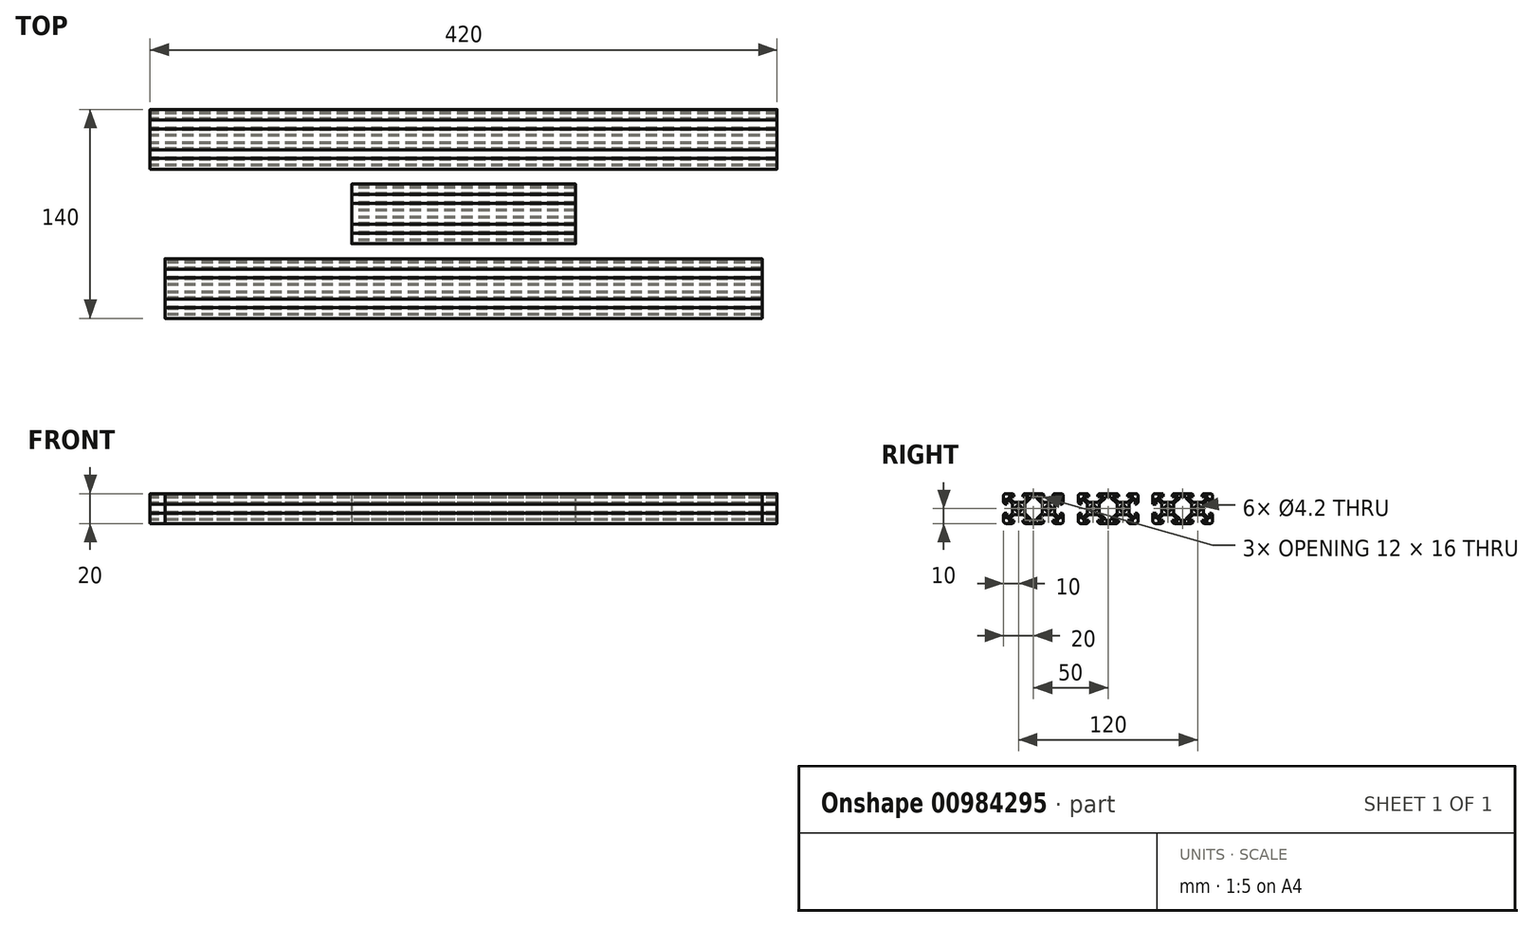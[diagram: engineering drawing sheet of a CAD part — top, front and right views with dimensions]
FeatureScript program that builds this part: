
annotation { "Feature Type Name" : "Feature", "Feature Type Description" : "" }
export const myFeature = defineFeature(function(context is Context, id is Id, definition is map)
    precondition{}
    {
        {
            var Q0;
            Q0=qCreatedBy(makeId("Right.planeOp"),FACE);
            var sketch = newSketch(context, id + "F0", { "sketchPlane" : qUnion([Q0])});
            skCircle(sketch, "E0", {"center": v(-10, 0) * mm, "radius": 2.1 * mm});
            skCircle(sketch, "E1", {"center": v(10, 0) * mm, "radius": 2.1 * mm});
            skPoint(sketch, "E2.middle", {"position": v(0, 0) * mm});
            skLineSegment(sketch, "E3.bottom", {"start": v(-14, 4) * mm, "end": v(-6, 4) * mm});
            skLineSegment(sketch, "E3.top", {"start": v(-14, -4) * mm, "end": v(-6, -4) * mm});
            skLineSegment(sketch, "E3.left", {"start": v(-14, 4) * mm, "end": v(-14, -4) * mm});
            skLineSegment(sketch, "E3.right", {"start": v(-6, 4) * mm, "end": v(-6, -4) * mm});
            skLineSegment(sketch, "E4.bottom", {"start": v(6, 4) * mm, "end": v(14, 4) * mm});
            skLineSegment(sketch, "E4.top", {"start": v(6, -4) * mm, "end": v(14, -4) * mm});
            skLineSegment(sketch, "E4.left", {"start": v(6, 4) * mm, "end": v(6, -4) * mm});
            skLineSegment(sketch, "E4.right", {"start": v(14, 4) * mm, "end": v(14, -4) * mm});
            skLineSegment(sketch, "E5.bottom", {"start": v(-20, 10) * mm, "end": v(20, 10) * mm});
            skLineSegment(sketch, "E5.top", {"start": v(-20, -10) * mm, "end": v(20, -10) * mm});
            skLineSegment(sketch, "E5.left", {"start": v(-20, 10) * mm, "end": v(-20, -10) * mm});
            skLineSegment(sketch, "E5.right", {"start": v(20, 10) * mm, "end": v(20, -10) * mm});
            skLineSegment(sketch, "E6", {"start": v(-20, 3) * mm, "end": v(-18, 3) * mm});
            skLineSegment(sketch, "E7", {"start": v(-18, 3) * mm, "end": v(-18, 7.08) * mm});
            skLineSegment(sketch, "E8", {"start": v(-18, 7.08) * mm, "end": v(-14, 3.08) * mm});
            skLineSegment(sketch, "E9", {"start": v(-13.08, 4) * mm, "end": v(-17.08, 8) * mm});
            skLineSegment(sketch, "E10", {"start": v(-17.08, 8) * mm, "end": v(-13, 8) * mm});
            skLineSegment(sketch, "E11", {"start": v(-13, 8) * mm, "end": v(-13, 10) * mm});
            skLineSegment(sketch, "E12", {"start": v(-14, -3.08) * mm, "end": v(-18, -7.08) * mm});
            skLineSegment(sketch, "E13", {"start": v(-18, -7.08) * mm, "end": v(-18, -3) * mm});
            skLineSegment(sketch, "E14", {"start": v(-18, -3) * mm, "end": v(-20, -3) * mm});
            skLineSegment(sketch, "E15", {"start": v(-13.08, -4) * mm, "end": v(-17.08, -8) * mm});
            skLineSegment(sketch, "E16", {"start": v(-17.08, -8) * mm, "end": v(-13, -8) * mm});
            skLineSegment(sketch, "E17", {"start": v(-13, -8) * mm, "end": v(-13, -10) * mm});
            skLineSegment(sketch, "E18", {"start": v(13.08, 4) * mm, "end": v(17.08, 8) * mm});
            skLineSegment(sketch, "E19", {"start": v(17.08, 8) * mm, "end": v(13, 8) * mm});
            skLineSegment(sketch, "E20", {"start": v(13, 8) * mm, "end": v(13, 10) * mm});
            skLineSegment(sketch, "E21", {"start": v(14, 3.08) * mm, "end": v(18, 7.08) * mm});
            skLineSegment(sketch, "E22", {"start": v(18, 7.08) * mm, "end": v(18, 3) * mm});
            skLineSegment(sketch, "E23", {"start": v(18, 3) * mm, "end": v(20, 3) * mm});
            skLineSegment(sketch, "E24", {"start": v(14, -3.08) * mm, "end": v(18, -7.08) * mm});
            skLineSegment(sketch, "E25", {"start": v(18, -7.08) * mm, "end": v(18, -3) * mm});
            skLineSegment(sketch, "E26", {"start": v(18, -3) * mm, "end": v(20, -3) * mm});
            skLineSegment(sketch, "E27", {"start": v(13.08, -4) * mm, "end": v(17.08, -8) * mm});
            skLineSegment(sketch, "E28", {"start": v(17.08, -8) * mm, "end": v(13, -8) * mm});
            skLineSegment(sketch, "E29", {"start": v(13, -8) * mm, "end": v(13, -10) * mm});
            skLineSegment(sketch, "E30", {"start": v(-6.92, 4) * mm, "end": v(-2.92, 8) * mm});
            skLineSegment(sketch, "E31", {"start": v(-2.92, 8) * mm, "end": v(-7, 8) * mm});
            skLineSegment(sketch, "E32", {"start": v(-7, 8) * mm, "end": v(-7, 10) * mm});
            skLineSegment(sketch, "E33", {"start": v(-6, 3.08) * mm, "end": v(-2, 7.08) * mm});
            skLineSegment(sketch, "E34", {"start": v(-6.92, -4) * mm, "end": v(-2.92, -8) * mm});
            skLineSegment(sketch, "E35", {"start": v(-2.92, -8) * mm, "end": v(-7, -8) * mm});
            skLineSegment(sketch, "E36", {"start": v(-7, -8) * mm, "end": v(-7, -10) * mm});
            skLineSegment(sketch, "E37", {"start": v(-6, -3.08) * mm, "end": v(-2, -7.08) * mm});
            skLineSegment(sketch, "E38", {"start": v(6.92, 4) * mm, "end": v(2.92, 8) * mm});
            skLineSegment(sketch, "E39", {"start": v(2.92, 8) * mm, "end": v(7, 8) * mm});
            skLineSegment(sketch, "E40", {"start": v(7, 8) * mm, "end": v(7, 10) * mm});
            skLineSegment(sketch, "E41", {"start": v(6, 3.08) * mm, "end": v(2, 7.08) * mm});
            skLineSegment(sketch, "E42", {"start": v(6.92, -4) * mm, "end": v(2.92, -8) * mm});
            skLineSegment(sketch, "E43", {"start": v(2.92, -8) * mm, "end": v(7, -8) * mm});
            skLineSegment(sketch, "E44", {"start": v(7, -8) * mm, "end": v(7, -10) * mm});
            skLineSegment(sketch, "E45", {"start": v(6, -3.08) * mm, "end": v(2, -7.08) * mm});
            skLineSegment(sketch, "E46", {"start": v(-2, 7.08) * mm, "end": v(-2, 8) * mm});
            skLineSegment(sketch, "E47", {"start": v(-2, 8) * mm, "end": v(2, 8) * mm});
            skLineSegment(sketch, "E48", {"start": v(2, 8) * mm, "end": v(2, 7.08) * mm});
            skLineSegment(sketch, "E49", {"start": v(2, -7.08) * mm, "end": v(2, -8) * mm});
            skLineSegment(sketch, "E50", {"start": v(2, -8) * mm, "end": v(-2.02, -8) * mm});
            skLineSegment(sketch, "E51", {"start": v(-2.02, -8) * mm, "end": v(-2, -7.08) * mm});
            skSolve(sketch);
        }
        {
            var Q0;
            {var subQ8=sQuery(id+"F0.wireOp",EDGE,"7Cvqsq3v-b1jp-Si3D-STMO-5d5Z4dZl0E6L");Q0=makeQuery(id+"F0.imprint","IMPRINT",FACE,{"disambiguationData":[TD([[makeQuery(id+"F0.imprint","IMPRINT",EDGE,{"derivedFrom":subQ8}),1.0]])]});}
            var Q1;
            Q1=makeQuery(id+"F0.imprint","IMPRINT",FACE,{"disambiguationData":[TD([[makeQuery(id+"F0.imprint","IMPRINT",EDGE,{"derivedFrom":sQuery(id+"F0.wireOp",EDGE,"E0")}),-1.0]])]});
            var Q2;
            Q2=makeQuery(id+"F0.imprint","IMPRINT",FACE,{"disambiguationData":[TD([[makeQuery(id+"F0.imprint","IMPRINT",EDGE,{"derivedFrom":sQuery(id+"F0.wireOp",EDGE,"E1")}),-1.0]])]});
            var Q3;
            {var subQ3=sQuery(id+"F0.wireOp",EDGE,"f1HrvhTk-PxuY-g1WT-5oFD-UpicsjZwxEBd.right");Q3=makeQuery(id+"F0.imprint","IMPRINT",FACE,{"disambiguationData":[TD([[makeQuery(id+"F0.imprint","IMPRINT",EDGE,{"derivedFrom":subQ3}),1.0]])]});}
            var Q4;
            {var subQ4=sQuery(id+"F0.wireOp",EDGE,"NmXkrHQB-t7IB-7fgh-WxZz-ZPCDYyFDkPix.top");Q4=makeQuery(id+"F0.imprint","IMPRINT",FACE,{"disambiguationData":[TD([[makeQuery(id+"F0.imprint","IMPRINT",EDGE,{"derivedFrom":subQ4}),1.0]])]});}
            var Q5;
            {var subQ9=sQuery(id+"F0.wireOp",EDGE,"jzImMTUU-LDJW-0Rce-YWhv-aavrS3r0fyrQ.right");Q5=makeQuery(id+"F0.imprint","IMPRINT",FACE,{"disambiguationData":[TD([[makeQuery(id+"F0.imprint","IMPRINT",EDGE,{"derivedFrom":subQ9}),1.0]])]});}
            var Q6;
            {var subQ8=sQuery(id+"F0.wireOp",EDGE,"S3BogOqV-sG4M-tAah-06HL-S0SJQAl7BcT5");Q6=makeQuery(id+"F0.imprint","IMPRINT",FACE,{"disambiguationData":[TD([[makeQuery(id+"F0.imprint","IMPRINT",EDGE,{"derivedFrom":subQ8}),1.0]])]});}
            var Q7;
            {var subQ0=sQuery(id+"F0.wireOp",EDGE,"jKtUflIW-kpum-jhkz-qf70-2aAi6vLTRXWU");Q7=makeQuery(id+"F0.imprint","IMPRINT",FACE,{"disambiguationData":[TD([[makeQuery(id+"F0.imprint","IMPRINT",EDGE,{"derivedFrom":subQ0}),1.0]])]});}
            var Q8;
            {var subQ5=sQuery(id+"F0.wireOp",EDGE,"gQbrqad4-Ddy9-TtRR-rflf-y5D3pQsQNXtq");Q8=makeQuery(id+"F0.imprint","IMPRINT",FACE,{"disambiguationData":[TD([[makeQuery(id+"F0.imprint","IMPRINT",EDGE,{"derivedFrom":subQ5}),-1.0]])]});}
            var Q9;
            {var subQ3=sQuery(id+"F0.wireOp",EDGE,"E6");Q9=makeQuery(id+"F0.imprint","IMPRINT",FACE,{"disambiguationData":[TD([[makeQuery(id+"F0.imprint","IMPRINT",EDGE,{"derivedFrom":subQ3}),1.0]])]});}
            var Q10;
            {var subQ9=sQuery(id+"F0.wireOp",EDGE,"E12");Q10=makeQuery(id+"F0.imprint","IMPRINT",FACE,{"disambiguationData":[TD([[makeQuery(id+"F0.imprint","IMPRINT",EDGE,{"derivedFrom":subQ9}),1.0]])]});}
            var Q11;
            {var subQ1=sQuery(id+"F0.wireOp",EDGE,"E34");Q11=makeQuery(id+"F0.imprint","IMPRINT",FACE,{"disambiguationData":[TD([[makeQuery(id+"F0.imprint","IMPRINT",EDGE,{"derivedFrom":subQ1}),1.0]])]});}
            var Q12;
            {var subQ7=sQuery(id+"F0.wireOp",EDGE,"E30");Q12=makeQuery(id+"F0.imprint","IMPRINT",FACE,{"disambiguationData":[TD([[makeQuery(id+"F0.imprint","IMPRINT",EDGE,{"derivedFrom":subQ7}),-1.0]])]});}
            var Q13;
            {var subQ9=sQuery(id+"F0.wireOp",EDGE,"E18");Q13=makeQuery(id+"F0.imprint","IMPRINT",FACE,{"disambiguationData":[TD([[makeQuery(id+"F0.imprint","IMPRINT",EDGE,{"derivedFrom":subQ9}),-1.0]])]});}
            var Q14;
            {var subQ9=sQuery(id+"F0.wireOp",EDGE,"E24");Q14=makeQuery(id+"F0.imprint","IMPRINT",FACE,{"disambiguationData":[TD([[makeQuery(id+"F0.imprint","IMPRINT",EDGE,{"derivedFrom":subQ9}),-1.0]])]});}
            extrude(context, id + "F1", {"entities" : qUnion([Q0, Q1, Q2, Q3, Q4, Q5, Q6, Q7, Q8, Q9, Q10, Q11, Q12, Q13, Q14]), "depth" : 75 * mm, "offsetDistance" : 25 * mm, "hasSecondDirection" : true, "secondDirectionOppositeDirection" : true, "secondDirectionDepth" : 75 * mm});
        }
        {
            var Q0;
            {var subQ3=sQuery(id+"F0.wireOp",EDGE,"E6");Q0=makeQuery(id+"F0.imprint","IMPRINT",FACE,{"disambiguationData":[TD([[makeQuery(id+"F0.imprint","IMPRINT",EDGE,{"derivedFrom":subQ3}),1.0]])]});}
            var Q1;
            Q1=makeQuery(id+"F0.imprint","IMPRINT",FACE,{"disambiguationData":[TD([[makeQuery(id+"F0.imprint","IMPRINT",EDGE,{"derivedFrom":sQuery(id+"F0.wireOp",EDGE,"E0")}),-1.0]])]});
            var Q2;
            {var subQ9=sQuery(id+"F0.wireOp",EDGE,"E12");Q2=makeQuery(id+"F0.imprint","IMPRINT",FACE,{"disambiguationData":[TD([[makeQuery(id+"F0.imprint","IMPRINT",EDGE,{"derivedFrom":subQ9}),1.0]])]});}
            var Q3;
            {var subQ1=sQuery(id+"F0.wireOp",EDGE,"E34");Q3=makeQuery(id+"F0.imprint","IMPRINT",FACE,{"disambiguationData":[TD([[makeQuery(id+"F0.imprint","IMPRINT",EDGE,{"derivedFrom":subQ1}),1.0]])]});}
            var Q4;
            {var subQ7=sQuery(id+"F0.wireOp",EDGE,"E30");Q4=makeQuery(id+"F0.imprint","IMPRINT",FACE,{"disambiguationData":[TD([[makeQuery(id+"F0.imprint","IMPRINT",EDGE,{"derivedFrom":subQ7}),-1.0]])]});}
            var Q5;
            {var subQ9=sQuery(id+"F0.wireOp",EDGE,"E18");Q5=makeQuery(id+"F0.imprint","IMPRINT",FACE,{"disambiguationData":[TD([[makeQuery(id+"F0.imprint","IMPRINT",EDGE,{"derivedFrom":subQ9}),-1.0]])]});}
            var Q6;
            {var subQ9=sQuery(id+"F0.wireOp",EDGE,"E24");Q6=makeQuery(id+"F0.imprint","IMPRINT",FACE,{"disambiguationData":[TD([[makeQuery(id+"F0.imprint","IMPRINT",EDGE,{"derivedFrom":subQ9}),-1.0]])]});}
            var Q7;
            Q7=makeQuery(id+"F0.imprint","IMPRINT",FACE,{"disambiguationData":[TD([[makeQuery(id+"F0.imprint","IMPRINT",EDGE,{"derivedFrom":sQuery(id+"F0.wireOp",EDGE,"E1")}),-1.0]])]});
            extrude(context, id + "F2", {"entities" : qUnion([Q0, Q1, Q2, Q3, Q4, Q5, Q6, Q7]), "depth" : 200 * mm, "offsetDistance" : 25 * mm, "hasSecondDirection" : true, "secondDirectionOppositeDirection" : true, "secondDirectionDepth" : 200 * mm});
        }
        {
            var Q0;
            {var subQ3=sQuery(id+"F0.wireOp",EDGE,"E6");Q0=makeQuery(id+"F0.imprint","IMPRINT",FACE,{"disambiguationData":[TD([[makeQuery(id+"F0.imprint","IMPRINT",EDGE,{"derivedFrom":subQ3}),1.0]])]});}
            var Q1;
            Q1=makeQuery(id+"F0.imprint","IMPRINT",FACE,{"disambiguationData":[TD([[makeQuery(id+"F0.imprint","IMPRINT",EDGE,{"derivedFrom":sQuery(id+"F0.wireOp",EDGE,"E0")}),-1.0]])]});
            var Q2;
            {var subQ9=sQuery(id+"F0.wireOp",EDGE,"E12");Q2=makeQuery(id+"F0.imprint","IMPRINT",FACE,{"disambiguationData":[TD([[makeQuery(id+"F0.imprint","IMPRINT",EDGE,{"derivedFrom":subQ9}),1.0]])]});}
            var Q3;
            {var subQ1=sQuery(id+"F0.wireOp",EDGE,"E34");Q3=makeQuery(id+"F0.imprint","IMPRINT",FACE,{"disambiguationData":[TD([[makeQuery(id+"F0.imprint","IMPRINT",EDGE,{"derivedFrom":subQ1}),1.0]])]});}
            var Q4;
            {var subQ7=sQuery(id+"F0.wireOp",EDGE,"E30");Q4=makeQuery(id+"F0.imprint","IMPRINT",FACE,{"disambiguationData":[TD([[makeQuery(id+"F0.imprint","IMPRINT",EDGE,{"derivedFrom":subQ7}),-1.0]])]});}
            var Q5;
            {var subQ9=sQuery(id+"F0.wireOp",EDGE,"E18");Q5=makeQuery(id+"F0.imprint","IMPRINT",FACE,{"disambiguationData":[TD([[makeQuery(id+"F0.imprint","IMPRINT",EDGE,{"derivedFrom":subQ9}),-1.0]])]});}
            var Q6;
            {var subQ9=sQuery(id+"F0.wireOp",EDGE,"E24");Q6=makeQuery(id+"F0.imprint","IMPRINT",FACE,{"disambiguationData":[TD([[makeQuery(id+"F0.imprint","IMPRINT",EDGE,{"derivedFrom":subQ9}),-1.0]])]});}
            var Q7;
            Q7=makeQuery(id+"F0.imprint","IMPRINT",FACE,{"disambiguationData":[TD([[makeQuery(id+"F0.imprint","IMPRINT",EDGE,{"derivedFrom":sQuery(id+"F0.wireOp",EDGE,"E1")}),-1.0]])]});
            extrude(context, id + "F3", {"entities" : qUnion([Q0, Q1, Q2, Q3, Q4, Q5, Q6, Q7]), "depth" : 210 * mm, "offsetDistance" : 25 * mm, "hasSecondDirection" : true, "secondDirectionOppositeDirection" : true, "secondDirectionDepth" : 210 * mm});
        }
        {
            var Q0;
            Q0=makeQuery(id+"F1.opExtrude","SWEPT_EDGE",EDGE,{"disambiguationData":[OSD([sQuery(id+"F0.wireOp",EDGE,"E5.bottom"),sQuery(id+"F0.wireOp",EDGE,"E5.right")])]});
            var Q1;
            Q1=makeQuery(id+"F1.opExtrude","SWEPT_EDGE",EDGE,{"disambiguationData":[OSD([sQuery(id+"F0.wireOp",EDGE,"E5.bottom"),sQuery(id+"F0.wireOp",EDGE,"E40")])]});
            var Q2;
            Q2=makeQuery(id+"F1.opExtrude","SWEPT_EDGE",EDGE,{"disambiguationData":[OSD([sQuery(id+"F0.wireOp",EDGE,"E5.bottom"),sQuery(id+"F0.wireOp",EDGE,"E20")])]});
            var Q3;
            Q3=makeQuery(id+"F1.opExtrude","SWEPT_EDGE",EDGE,{"disambiguationData":[OSD([sQuery(id+"F0.wireOp",EDGE,"E5.bottom"),sQuery(id+"F0.wireOp",EDGE,"E32")])]});
            var Q4;
            Q4=makeQuery(id+"F1.opExtrude","SWEPT_EDGE",EDGE,{"disambiguationData":[OSD([sQuery(id+"F0.wireOp",EDGE,"E5.bottom"),sQuery(id+"F0.wireOp",EDGE,"E11")])]});
            var Q5;
            Q5=makeQuery(id+"F1.opExtrude","SWEPT_EDGE",EDGE,{"disambiguationData":[OSD([sQuery(id+"F0.wireOp",EDGE,"E5.bottom"),sQuery(id+"F0.wireOp",EDGE,"E5.left")])]});
            var Q6;
            Q6=makeQuery(id+"F1.opExtrude","SWEPT_EDGE",EDGE,{"disambiguationData":[OSD([sQuery(id+"F0.wireOp",EDGE,"E5.left"),sQuery(id+"F0.wireOp",EDGE,"E6")])]});
            var Q7;
            Q7=makeQuery(id+"F1.opExtrude","SWEPT_EDGE",EDGE,{"disambiguationData":[OSD([sQuery(id+"F0.wireOp",EDGE,"E5.left"),sQuery(id+"F0.wireOp",EDGE,"E14")])]});
            var Q8;
            Q8=makeQuery(id+"F1.opExtrude","SWEPT_EDGE",EDGE,{"disambiguationData":[OSD([sQuery(id+"F0.wireOp",EDGE,"E5.top"),sQuery(id+"F0.wireOp",EDGE,"E5.left")])]});
            var Q9;
            Q9=makeQuery(id+"F1.opExtrude","SWEPT_EDGE",EDGE,{"disambiguationData":[OSD([sQuery(id+"F0.wireOp",EDGE,"E5.top"),sQuery(id+"F0.wireOp",EDGE,"E17")])]});
            var Q10;
            Q10=makeQuery(id+"F1.opExtrude","SWEPT_EDGE",EDGE,{"disambiguationData":[OSD([sQuery(id+"F0.wireOp",EDGE,"E5.top"),sQuery(id+"F0.wireOp",EDGE,"E36")])]});
            var Q11;
            Q11=makeQuery(id+"F1.opExtrude","SWEPT_EDGE",EDGE,{"disambiguationData":[OSD([sQuery(id+"F0.wireOp",EDGE,"E5.top"),sQuery(id+"F0.wireOp",EDGE,"E44")])]});
            var Q12;
            Q12=makeQuery(id+"F1.opExtrude","SWEPT_EDGE",EDGE,{"disambiguationData":[OSD([sQuery(id+"F0.wireOp",EDGE,"E5.top"),sQuery(id+"F0.wireOp",EDGE,"E5.right")])]});
            var Q13;
            Q13=makeQuery(id+"F1.opExtrude","SWEPT_EDGE",EDGE,{"disambiguationData":[OSD([sQuery(id+"F0.wireOp",EDGE,"E5.right"),sQuery(id+"F0.wireOp",EDGE,"E26")])]});
            var Q14;
            Q14=makeQuery(id+"F1.opExtrude","SWEPT_EDGE",EDGE,{"disambiguationData":[OSD([sQuery(id+"F0.wireOp",EDGE,"E5.right"),sQuery(id+"F0.wireOp",EDGE,"E23")])]});
            var Q15;
            Q15=makeQuery(id+"F1.opExtrude","SWEPT_EDGE",EDGE,{"disambiguationData":[OSD([sQuery(id+"F0.wireOp",EDGE,"E5.top"),sQuery(id+"F0.wireOp",EDGE,"E29")])]});
            var Q16;
            Q16=makeQuery(id+"F3.opExtrude","SWEPT_EDGE",EDGE,{"disambiguationData":[OSD([sQuery(id+"F0.wireOp",EDGE,"E5.bottom"),sQuery(id+"F0.wireOp",EDGE,"E5.left")])]});
            var Q17;
            Q17=makeQuery(id+"F3.opExtrude","SWEPT_EDGE",EDGE,{"disambiguationData":[OSD([sQuery(id+"F0.wireOp",EDGE,"E5.top"),sQuery(id+"F0.wireOp",EDGE,"E5.left")])]});
            var Q18;
            Q18=makeQuery(id+"F3.opExtrude","SWEPT_EDGE",EDGE,{"disambiguationData":[OSD([sQuery(id+"F0.wireOp",EDGE,"E5.top"),sQuery(id+"F0.wireOp",EDGE,"E36")])]});
            var Q19;
            Q19=makeQuery(id+"F3.opExtrude","SWEPT_EDGE",EDGE,{"disambiguationData":[OSD([sQuery(id+"F0.wireOp",EDGE,"E5.bottom"),sQuery(id+"F0.wireOp",EDGE,"E32")])]});
            var Q20;
            Q20=makeQuery(id+"F3.opExtrude","SWEPT_EDGE",EDGE,{"disambiguationData":[OSD([sQuery(id+"F0.wireOp",EDGE,"E5.bottom"),sQuery(id+"F0.wireOp",EDGE,"E20")])]});
            var Q21;
            Q21=makeQuery(id+"F3.opExtrude","SWEPT_EDGE",EDGE,{"disambiguationData":[OSD([sQuery(id+"F0.wireOp",EDGE,"E5.bottom"),sQuery(id+"F0.wireOp",EDGE,"E40")])]});
            var Q22;
            Q22=makeQuery(id+"F3.opExtrude","SWEPT_EDGE",EDGE,{"disambiguationData":[OSD([sQuery(id+"F0.wireOp",EDGE,"E5.bottom"),sQuery(id+"F0.wireOp",EDGE,"E5.right")])]});
            var Q23;
            Q23=makeQuery(id+"F3.opExtrude","SWEPT_EDGE",EDGE,{"disambiguationData":[OSD([sQuery(id+"F0.wireOp",EDGE,"E5.right"),sQuery(id+"F0.wireOp",EDGE,"E23")])]});
            var Q24;
            Q24=makeQuery(id+"F3.opExtrude","SWEPT_EDGE",EDGE,{"disambiguationData":[OSD([sQuery(id+"F0.wireOp",EDGE,"E5.right"),sQuery(id+"F0.wireOp",EDGE,"E26")])]});
            var Q25;
            Q25=makeQuery(id+"F3.opExtrude","SWEPT_EDGE",EDGE,{"disambiguationData":[OSD([sQuery(id+"F0.wireOp",EDGE,"E5.top"),sQuery(id+"F0.wireOp",EDGE,"E5.right")])]});
            var Q26;
            Q26=makeQuery(id+"F3.opExtrude","SWEPT_EDGE",EDGE,{"disambiguationData":[OSD([sQuery(id+"F0.wireOp",EDGE,"E5.top"),sQuery(id+"F0.wireOp",EDGE,"E29")])]});
            var Q27;
            Q27=makeQuery(id+"F3.opExtrude","SWEPT_EDGE",EDGE,{"disambiguationData":[OSD([sQuery(id+"F0.wireOp",EDGE,"E5.top"),sQuery(id+"F0.wireOp",EDGE,"E44")])]});
            var Q28;
            Q28=makeQuery(id+"F3.opExtrude","SWEPT_EDGE",EDGE,{"disambiguationData":[OSD([sQuery(id+"F0.wireOp",EDGE,"E5.top"),sQuery(id+"F0.wireOp",EDGE,"E17")])]});
            var Q29;
            Q29=makeQuery(id+"F2.opExtrude","SWEPT_EDGE",EDGE,{"disambiguationData":[OSD([sQuery(id+"F0.wireOp",EDGE,"E5.bottom"),sQuery(id+"F0.wireOp",EDGE,"E5.left")])]});
            var Q30;
            Q30=makeQuery(id+"F2.opExtrude","SWEPT_EDGE",EDGE,{"disambiguationData":[OSD([sQuery(id+"F0.wireOp",EDGE,"E5.bottom"),sQuery(id+"F0.wireOp",EDGE,"E11")])]});
            var Q31;
            Q31=makeQuery(id+"F2.opExtrude","SWEPT_EDGE",EDGE,{"disambiguationData":[OSD([sQuery(id+"F0.wireOp",EDGE,"E5.bottom"),sQuery(id+"F0.wireOp",EDGE,"E32")])]});
            var Q32;
            Q32=makeQuery(id+"F2.opExtrude","SWEPT_EDGE",EDGE,{"disambiguationData":[OSD([sQuery(id+"F0.wireOp",EDGE,"E5.bottom"),sQuery(id+"F0.wireOp",EDGE,"E40")])]});
            var Q33;
            Q33=makeQuery(id+"F2.opExtrude","SWEPT_EDGE",EDGE,{"disambiguationData":[OSD([sQuery(id+"F0.wireOp",EDGE,"E5.bottom"),sQuery(id+"F0.wireOp",EDGE,"E5.right")])]});
            var Q34;
            Q34=makeQuery(id+"F2.opExtrude","SWEPT_EDGE",EDGE,{"disambiguationData":[OSD([sQuery(id+"F0.wireOp",EDGE,"E5.bottom"),sQuery(id+"F0.wireOp",EDGE,"E20")])]});
            var Q35;
            Q35=makeQuery(id+"F2.opExtrude","SWEPT_EDGE",EDGE,{"disambiguationData":[OSD([sQuery(id+"F0.wireOp",EDGE,"E5.left"),sQuery(id+"F0.wireOp",EDGE,"E14")])]});
            var Q36;
            Q36=makeQuery(id+"F2.opExtrude","SWEPT_EDGE",EDGE,{"disambiguationData":[OSD([sQuery(id+"F0.wireOp",EDGE,"E5.right"),sQuery(id+"F0.wireOp",EDGE,"E26")])]});
            var Q37;
            Q37=makeQuery(id+"F2.opExtrude","SWEPT_EDGE",EDGE,{"disambiguationData":[OSD([sQuery(id+"F0.wireOp",EDGE,"E5.top"),sQuery(id+"F0.wireOp",EDGE,"E29")])]});
            var Q38;
            Q38=makeQuery(id+"F2.opExtrude","SWEPT_EDGE",EDGE,{"disambiguationData":[OSD([sQuery(id+"F0.wireOp",EDGE,"E5.top"),sQuery(id+"F0.wireOp",EDGE,"E36")])]});
            var Q39;
            Q39=makeQuery(id+"F2.opExtrude","SWEPT_EDGE",EDGE,{"disambiguationData":[OSD([sQuery(id+"F0.wireOp",EDGE,"E5.right"),sQuery(id+"F0.wireOp",EDGE,"E23")])]});
            var Q40;
            Q40=makeQuery(id+"F2.opExtrude","SWEPT_EDGE",EDGE,{"disambiguationData":[OSD([sQuery(id+"F0.wireOp",EDGE,"E5.top"),sQuery(id+"F0.wireOp",EDGE,"E5.right")])]});
            var Q41;
            Q41=makeQuery(id+"F2.opExtrude","SWEPT_EDGE",EDGE,{"disambiguationData":[OSD([sQuery(id+"F0.wireOp",EDGE,"E5.top"),sQuery(id+"F0.wireOp",EDGE,"E44")])]});
            var Q42;
            Q42=makeQuery(id+"F2.opExtrude","SWEPT_EDGE",EDGE,{"disambiguationData":[OSD([sQuery(id+"F0.wireOp",EDGE,"E5.top"),sQuery(id+"F0.wireOp",EDGE,"E17")])]});
            var Q43;
            Q43=makeQuery(id+"F2.opExtrude","SWEPT_EDGE",EDGE,{"disambiguationData":[OSD([sQuery(id+"F0.wireOp",EDGE,"E5.top"),sQuery(id+"F0.wireOp",EDGE,"E5.left")])]});
            var Q44;
            Q44=makeQuery(id+"F2.opExtrude","SWEPT_EDGE",EDGE,{"disambiguationData":[OSD([sQuery(id+"F0.wireOp",EDGE,"E5.left"),sQuery(id+"F0.wireOp",EDGE,"E6")])]});
            fillet(context, id + "F4", {"entities" : qUnion([Q0, Q1, Q2, Q3, Q4, Q5, Q6, Q7, Q8, Q9, Q10, Q11, Q12, Q13, Q14, Q15, Q16, Q17, Q18, Q19, Q20, Q21, Q22, Q23, Q24, Q25, Q26, Q27, Q28, Q29, Q30, Q31, Q32, Q33, Q34, Q35, Q36, Q37, Q38, Q39, Q40, Q41, Q42, Q43, Q44]), "radius" : 1.5 * mm, "tangentPropagation" : true, "allowEdgeOverflow" : false});
        }
        {
            var Q0;
            Q0=makeQuery(id+"F3.opExtrude","SWEPT_BODY",BODY,{"disambiguationData":[OSD([sQuery(id+"F0.wireOp",EDGE,"E0"),sQuery(id+"F0.wireOp",EDGE,"E1"),sQuery(id+"F0.wireOp",EDGE,"E3.bottom"),sQuery(id+"F0.wireOp",EDGE,"E3.top"),sQuery(id+"F0.wireOp",EDGE,"E3.left"),sQuery(id+"F0.wireOp",EDGE,"E3.right"),sQuery(id+"F0.wireOp",EDGE,"E4.bottom"),sQuery(id+"F0.wireOp",EDGE,"E4.top"),sQuery(id+"F0.wireOp",EDGE,"E4.left"),sQuery(id+"F0.wireOp",EDGE,"E4.right"),sQuery(id+"F0.wireOp",EDGE,"E5.bottom"),sQuery(id+"F0.wireOp",EDGE,"E5.top"),sQuery(id+"F0.wireOp",EDGE,"E5.left"),sQuery(id+"F0.wireOp",EDGE,"E5.right"),sQuery(id+"F0.wireOp",EDGE,"E6"),sQuery(id+"F0.wireOp",EDGE,"E7"),sQuery(id+"F0.wireOp",EDGE,"E8"),sQuery(id+"F0.wireOp",EDGE,"E9"),sQuery(id+"F0.wireOp",EDGE,"E10"),sQuery(id+"F0.wireOp",EDGE,"E11"),sQuery(id+"F0.wireOp",EDGE,"E12"),sQuery(id+"F0.wireOp",EDGE,"E13"),sQuery(id+"F0.wireOp",EDGE,"E14"),sQuery(id+"F0.wireOp",EDGE,"E15"),sQuery(id+"F0.wireOp",EDGE,"E16"),sQuery(id+"F0.wireOp",EDGE,"E17"),sQuery(id+"F0.wireOp",EDGE,"E18"),sQuery(id+"F0.wireOp",EDGE,"E19"),sQuery(id+"F0.wireOp",EDGE,"E20"),sQuery(id+"F0.wireOp",EDGE,"E21"),sQuery(id+"F0.wireOp",EDGE,"E22"),sQuery(id+"F0.wireOp",EDGE,"E23"),sQuery(id+"F0.wireOp",EDGE,"E24"),sQuery(id+"F0.wireOp",EDGE,"E25"),sQuery(id+"F0.wireOp",EDGE,"E26"),sQuery(id+"F0.wireOp",EDGE,"E27"),sQuery(id+"F0.wireOp",EDGE,"E28"),sQuery(id+"F0.wireOp",EDGE,"E29"),sQuery(id+"F0.wireOp",EDGE,"E30"),sQuery(id+"F0.wireOp",EDGE,"E31"),sQuery(id+"F0.wireOp",EDGE,"E32"),sQuery(id+"F0.wireOp",EDGE,"E33"),sQuery(id+"F0.wireOp",EDGE,"E34"),sQuery(id+"F0.wireOp",EDGE,"E35"),sQuery(id+"F0.wireOp",EDGE,"E36"),sQuery(id+"F0.wireOp",EDGE,"E37"),sQuery(id+"F0.wireOp",EDGE,"E38"),sQuery(id+"F0.wireOp",EDGE,"E39"),sQuery(id+"F0.wireOp",EDGE,"E40"),sQuery(id+"F0.wireOp",EDGE,"E41"),sQuery(id+"F0.wireOp",EDGE,"E42"),sQuery(id+"F0.wireOp",EDGE,"E43"),sQuery(id+"F0.wireOp",EDGE,"E44"),sQuery(id+"F0.wireOp",EDGE,"E45"),sQuery(id+"F0.wireOp",EDGE,"E46"),sQuery(id+"F0.wireOp",EDGE,"E47"),sQuery(id+"F0.wireOp",EDGE,"E48"),sQuery(id+"F0.wireOp",EDGE,"E49"),sQuery(id+"F0.wireOp",EDGE,"E50"),sQuery(id+"F0.wireOp",EDGE,"E51")])]});
            transform(context, id + "F5", {"entities" : qUnion([Q0]), "transformType" : TransformType.TRANSLATION_3D, "dx" : 0 * mm, "dy" : 50 * mm, "dz" : 0 * mm, "makeCopy" : false});
        }
        {
            var Q0;
            Q0=makeQuery(id+"F2.opExtrude","SWEPT_BODY",BODY,{"disambiguationData":[OSD([sQuery(id+"F0.wireOp",EDGE,"E0"),sQuery(id+"F0.wireOp",EDGE,"E1"),sQuery(id+"F0.wireOp",EDGE,"E3.bottom"),sQuery(id+"F0.wireOp",EDGE,"E3.top"),sQuery(id+"F0.wireOp",EDGE,"E3.left"),sQuery(id+"F0.wireOp",EDGE,"E3.right"),sQuery(id+"F0.wireOp",EDGE,"E4.bottom"),sQuery(id+"F0.wireOp",EDGE,"E4.top"),sQuery(id+"F0.wireOp",EDGE,"E4.left"),sQuery(id+"F0.wireOp",EDGE,"E4.right"),sQuery(id+"F0.wireOp",EDGE,"E5.bottom"),sQuery(id+"F0.wireOp",EDGE,"E5.top"),sQuery(id+"F0.wireOp",EDGE,"E5.left"),sQuery(id+"F0.wireOp",EDGE,"E5.right"),sQuery(id+"F0.wireOp",EDGE,"E6"),sQuery(id+"F0.wireOp",EDGE,"E7"),sQuery(id+"F0.wireOp",EDGE,"E8"),sQuery(id+"F0.wireOp",EDGE,"E9"),sQuery(id+"F0.wireOp",EDGE,"E10"),sQuery(id+"F0.wireOp",EDGE,"E11"),sQuery(id+"F0.wireOp",EDGE,"E12"),sQuery(id+"F0.wireOp",EDGE,"E13"),sQuery(id+"F0.wireOp",EDGE,"E14"),sQuery(id+"F0.wireOp",EDGE,"E15"),sQuery(id+"F0.wireOp",EDGE,"E16"),sQuery(id+"F0.wireOp",EDGE,"E17"),sQuery(id+"F0.wireOp",EDGE,"E18"),sQuery(id+"F0.wireOp",EDGE,"E19"),sQuery(id+"F0.wireOp",EDGE,"E20"),sQuery(id+"F0.wireOp",EDGE,"E21"),sQuery(id+"F0.wireOp",EDGE,"E22"),sQuery(id+"F0.wireOp",EDGE,"E23"),sQuery(id+"F0.wireOp",EDGE,"E24"),sQuery(id+"F0.wireOp",EDGE,"E25"),sQuery(id+"F0.wireOp",EDGE,"E26"),sQuery(id+"F0.wireOp",EDGE,"E27"),sQuery(id+"F0.wireOp",EDGE,"E28"),sQuery(id+"F0.wireOp",EDGE,"E29"),sQuery(id+"F0.wireOp",EDGE,"E30"),sQuery(id+"F0.wireOp",EDGE,"E31"),sQuery(id+"F0.wireOp",EDGE,"E32"),sQuery(id+"F0.wireOp",EDGE,"E33"),sQuery(id+"F0.wireOp",EDGE,"E34"),sQuery(id+"F0.wireOp",EDGE,"E35"),sQuery(id+"F0.wireOp",EDGE,"E36"),sQuery(id+"F0.wireOp",EDGE,"E37"),sQuery(id+"F0.wireOp",EDGE,"E38"),sQuery(id+"F0.wireOp",EDGE,"E39"),sQuery(id+"F0.wireOp",EDGE,"E40"),sQuery(id+"F0.wireOp",EDGE,"E41"),sQuery(id+"F0.wireOp",EDGE,"E42"),sQuery(id+"F0.wireOp",EDGE,"E43"),sQuery(id+"F0.wireOp",EDGE,"E44"),sQuery(id+"F0.wireOp",EDGE,"E45"),sQuery(id+"F0.wireOp",EDGE,"E46"),sQuery(id+"F0.wireOp",EDGE,"E47"),sQuery(id+"F0.wireOp",EDGE,"E48"),sQuery(id+"F0.wireOp",EDGE,"E49"),sQuery(id+"F0.wireOp",EDGE,"E50"),sQuery(id+"F0.wireOp",EDGE,"E51")])]});
            transform(context, id + "F6", {"entities" : qUnion([Q0]), "transformType" : TransformType.TRANSLATION_3D, "dx" : 0 * mm, "dy" : -50 * mm, "dz" : 0 * mm, "makeCopy" : false});
        }
    });
